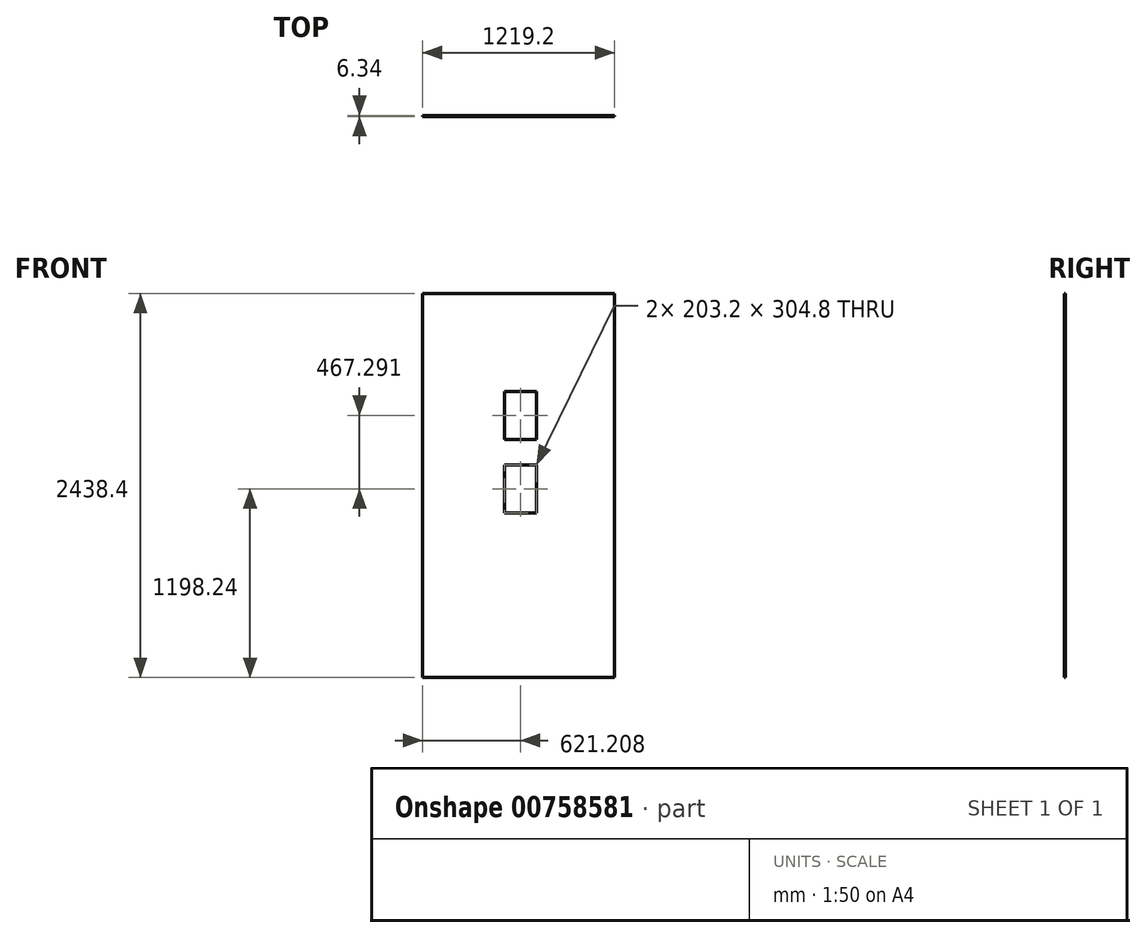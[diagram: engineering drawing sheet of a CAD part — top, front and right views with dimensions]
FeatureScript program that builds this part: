
annotation { "Feature Type Name" : "Feature", "Feature Type Description" : "" }
export const myFeature = defineFeature(function(context is Context, id is Id, definition is map)
    precondition{}
    {
        {
            var Q0;
            Q0=qCreatedBy(makeId("Front.planeOp"),FACE);
            var sketch = newSketch(context, id + "F0", { "sketchPlane" : qUnion([Q0])});
            skLineSegment(sketch, "E0.bottom", {"start": v(-609.6, 1219.2) * mm, "end": v(609.6, 1219.2) * mm});
            skLineSegment(sketch, "E0.top", {"start": v(-609.6, -1219.2) * mm, "end": v(609.6, -1219.2) * mm});
            skLineSegment(sketch, "E0.left", {"start": v(-609.6, 1219.2) * mm, "end": v(-609.6, -1219.2) * mm});
            skLineSegment(sketch, "E0.right", {"start": v(609.6, 1219.2) * mm, "end": v(609.6, -1219.2) * mm});
            skPoint(sketch, "E0.middle", {"position": v(0, 0) * mm});
            skLineSegment(sketch, "E1.bottom", {"start": v(-90, 598.73) * mm, "end": v(113.2, 598.73) * mm});
            skLineSegment(sketch, "E1.top", {"start": v(-90, 293.93) * mm, "end": v(113.2, 293.93) * mm});
            skLineSegment(sketch, "E1.left", {"start": v(-90, 598.73) * mm, "end": v(-90, 293.93) * mm});
            skLineSegment(sketch, "E1.right", {"start": v(113.2, 598.73) * mm, "end": v(113.2, 293.93) * mm});
            skLineSegment(sketch, "E2.bottom", {"start": v(-90, 131.44) * mm, "end": v(113.2, 131.44) * mm});
            skLineSegment(sketch, "E2.top", {"start": v(-90, -173.36) * mm, "end": v(113.2, -173.36) * mm});
            skLineSegment(sketch, "E2.left", {"start": v(-90, 131.44) * mm, "end": v(-90, -173.36) * mm});
            skLineSegment(sketch, "E2.right", {"start": v(113.2, 131.44) * mm, "end": v(113.2, -173.36) * mm});
            skSolve(sketch);
        }
        {
            var Q0;
            Q0=makeQuery(id+"F0.imprint","IMPRINT",FACE,{"disambiguationData":[TD([[makeQuery(id+"F0.imprint","IMPRINT",EDGE,{"derivedFrom":sQuery(id+"F0.wireOp",EDGE,"E0.bottom")}),-1.0]])]});
            extrude(context, id + "F1", {"entities" : qUnion([Q0]), "endBound" : BoundingType.SYMMETRIC, "depth" : 6.35 * mm, "offsetDistance" : 25.4 * mm});
        }
    });
